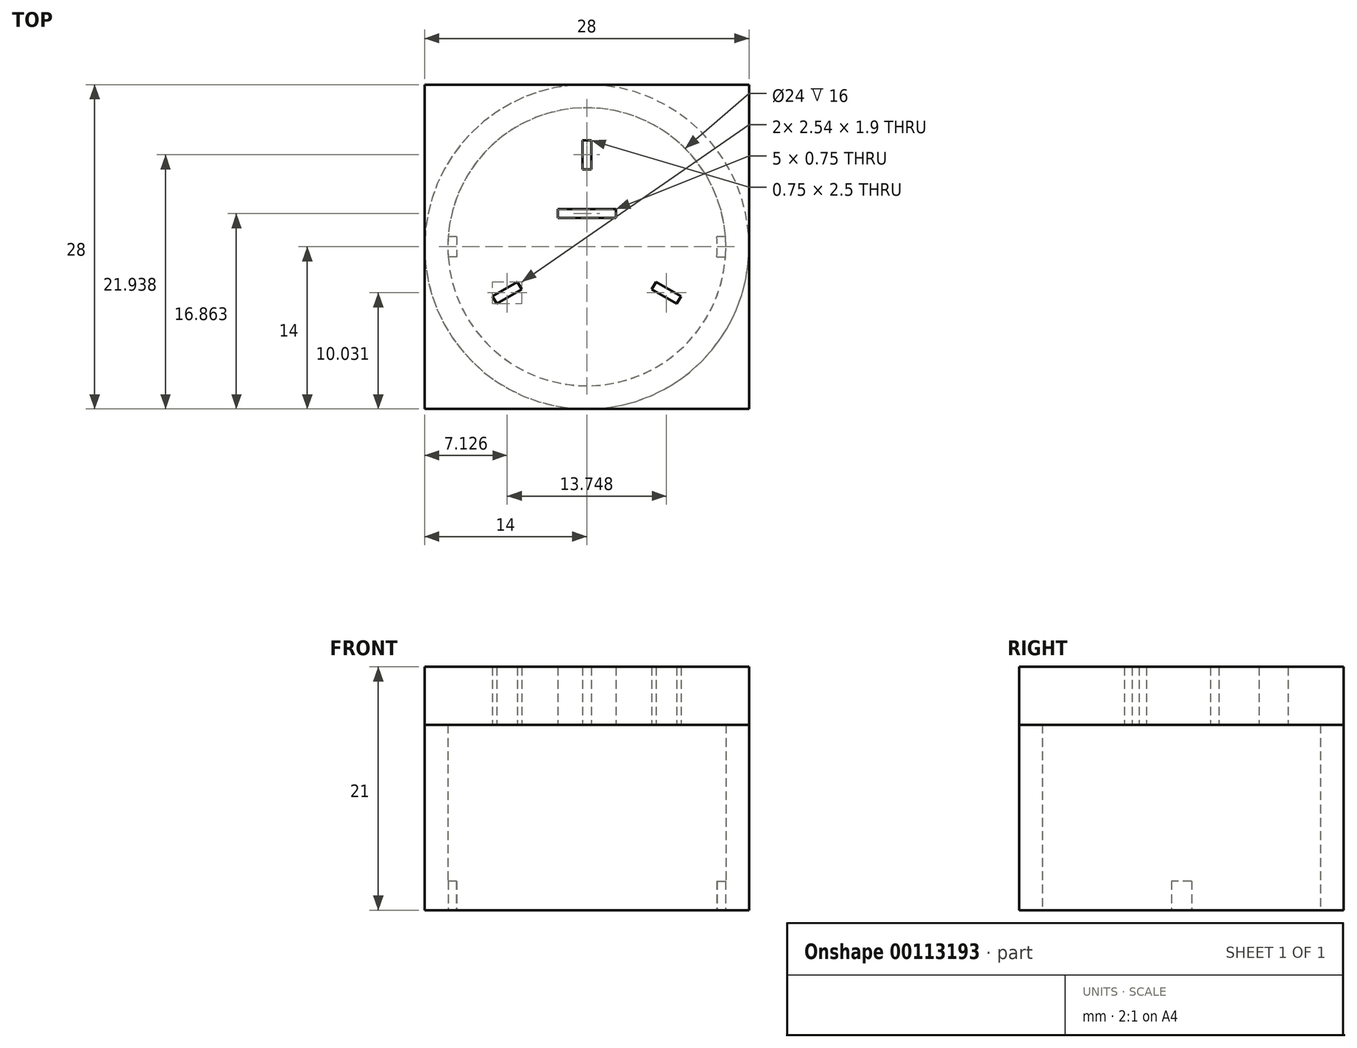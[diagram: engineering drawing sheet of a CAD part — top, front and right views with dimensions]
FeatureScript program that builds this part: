
annotation { "Feature Type Name" : "Feature", "Feature Type Description" : "" }
export const myFeature = defineFeature(function(context is Context, id is Id, definition is map)
    precondition{}
    {
        {
            var Q0;
            Q0=qCreatedBy(makeId("Top.planeOp"),FACE);
            var sketch = newSketch(context, id + "F0", { "sketchPlane" : qUnion([Q0])});
            skCircle(sketch, "E0", {"center": v(0, 0) * mm, "radius": 12 * mm});
            skCircle(sketch, "E1.0", {"center": v(0, 0) * mm, "radius": 14 * mm});
            skSolve(sketch);
        }
        {
            var Q0;
            Q0=makeQuery(id+"F0.imprint","IMPRINT",FACE,{"disambiguationData":[TD([[makeQuery(id+"F0.imprint","IMPRINT",EDGE,{"derivedFrom":sQuery(id+"F0.wireOp",EDGE,"E0")}),-1.0]])]});
            extrude(context, id + "F1", {"entities" : qUnion([Q0]), "depth" : 16 * mm});
        }
        {
            var Q0;
            Q0=qCreatedBy(makeId("Top.planeOp"),FACE);
            var sketch = newSketch(context, id + "F2", { "sketchPlane" : qUnion([Q0])});
            skLineSegment(sketch, "E2", {"start": v(12, 0) * mm, "end": v(-12, 0) * mm, "construction": true});
            skArc(sketch, "E3.0", {"start": v(-11.97, 0.87) * mm, "mid": v(-12, 0) * mm, "end": v(-11.97, -0.87) * mm});
            skLineSegment(sketch, "E4", {"start": v(11.97, 0.88) * mm, "end": v(11.22, 0.88) * mm});
            skLineSegment(sketch, "E5", {"start": v(11.22, -0.88) * mm, "end": v(11.97, -0.88) * mm});
            skArc(sketch, "E6", {"start": v(-11.22, 0.87) * mm, "mid": v(-11.25, 0) * mm, "end": v(-11.22, -0.87) * mm});
            skLineSegment(sketch, "E7", {"start": v(-11.22, 0.88) * mm, "end": v(-11.97, 0.88) * mm});
            skLineSegment(sketch, "E8", {"start": v(-11.22, -0.88) * mm, "end": v(-11.97, -0.88) * mm});
            skLineSegment(sketch, "E9", {"start": v(11.6, 0.87) * mm, "end": v(11.6, -0.88) * mm, "construction": true});
            skPoint(sketch, "E10", {"position": v(11.6, 0) * mm});
            skArc(sketch, "E11.trimOffspring", {"start": v(11.97, -0.87) * mm, "mid": v(12, 0) * mm, "end": v(11.97, 0.87) * mm});
            skArc(sketch, "E12.trimOffspring", {"start": v(11.22, -0.87) * mm, "mid": v(11.25, 0) * mm, "end": v(11.22, 0.88) * mm});
            skSolve(sketch);
        }
        {
            var Q0;
            Q0 = qSketchRegion(id + "F2", true);
            extrude(context, id + "F3", {"entities" : qUnion([Q0]), "operationType" : NewBodyOperationType.ADD, "depth" : 2.5 * mm});
        }
        {
            var Q0;
            Q0=makeQuery(id+"F1.opExtrude","CAP_FACE",FACE,{"disambiguationData":[OSD([sQuery(id+"F0.wireOp",EDGE,"E0"),sQuery(id+"F0.wireOp",EDGE,"E1.0")])],"isStart":false});
            var sketch = newSketch(context, id + "F4", { "sketchPlane" : qUnion([Q0])});
            skLineSegment(sketch, "E13.bottom", {"start": v(-14, -14) * mm, "end": v(14, -14) * mm});
            skLineSegment(sketch, "E13.top", {"start": v(-14, 14) * mm, "end": v(14, 14) * mm});
            skLineSegment(sketch, "E13.left", {"start": v(-14, -14) * mm, "end": v(-14, 14) * mm});
            skLineSegment(sketch, "E13.right", {"start": v(14, -14) * mm, "end": v(14, 14) * mm});
            skPoint(sketch, "E13.middle", {"position": v(0, 0) * mm});
            skSolve(sketch);
        }
        {
            var Q0;
            Q0 = qSketchRegion(id + "F4", true);
            extrude(context, id + "F5", {"entities" : qUnion([Q0]), "operationType" : NewBodyOperationType.ADD, "depth" : 5 * mm});
        }
        {
            var Q0;
            Q0=makeQuery(id+"F5.boolean.opBoolean","SPLIT",FACE,{"disambiguationData":[TD([makeQuery(id+"F1.opExtrude","SWEPT_FACE",FACE,{"disambiguationData":[OSD([sQuery(id+"F0.wireOp",EDGE,"E0")])]})])],"derivedFrom":makeQuery(id+"F5.opExtrude","CAP_FACE",FACE,{"disambiguationData":[OSD([sQuery(id+"F4.wireOp",EDGE,"E13.bottom"),sQuery(id+"F4.wireOp",EDGE,"E13.top"),sQuery(id+"F4.wireOp",EDGE,"E13.left"),sQuery(id+"F4.wireOp",EDGE,"E13.right")])],"isStart":true})});
            var sketch = newSketch(context, id + "F6", { "sketchPlane" : qUnion([Q0])});
            skLineSegment(sketch, "E14", {"start": v(0, 0) * mm, "end": v(0, -12) * mm, "construction": true});
            skCircle(sketch, "E15", {"center": v(0, 0) * mm, "radius": 4.92 * mm, "construction": true});
            skCircle(sketch, "E16", {"center": v(0, 0) * mm, "radius": 9.53 * mm, "construction": true});
            skCircle(sketch, "E17", {"center": v(0, 0) * mm, "radius": 6.35 * mm, "construction": true});
            skLineSegment(sketch, "E18.bottom", {"start": v(2.5, -2.49) * mm, "end": v(-2.5, -2.49) * mm});
            skLineSegment(sketch, "E18.top", {"start": v(2.5, -3.24) * mm, "end": v(-2.5, -3.24) * mm});
            skLineSegment(sketch, "E18.left", {"start": v(2.5, -2.49) * mm, "end": v(2.5, -3.24) * mm});
            skLineSegment(sketch, "E18.right", {"start": v(-2.5, -2.49) * mm, "end": v(-2.5, -3.24) * mm});
            skPoint(sketch, "E18.middle", {"position": v(0, -2.86) * mm});
            skLineSegment(sketch, "E19.bottom", {"start": v(0.38, -9.19) * mm, "end": v(-0.37, -9.19) * mm});
            skLineSegment(sketch, "E19.top", {"start": v(0.38, -6.69) * mm, "end": v(-0.37, -6.69) * mm});
            skLineSegment(sketch, "E19.left", {"start": v(0.37, -9.19) * mm, "end": v(0.37, -6.69) * mm});
            skLineSegment(sketch, "E19.right", {"start": v(-0.38, -9.19) * mm, "end": v(-0.38, -6.69) * mm});
            skPoint(sketch, "E19.middle", {"position": v(0, -7.94) * mm});
            skLineSegment(sketch, "E20", {"start": v(0, -6.35) * mm, "end": v(0, -9.53) * mm});
            skLineSegment(sketch, "E21.1.0", {"start": v(5.5, 3.17) * mm, "end": v(8.25, 4.76) * mm});
            skLineSegment(sketch, "E21.1.1", {"start": v(8.14, 4.27) * mm, "end": v(5.98, 3.02) * mm});
            skLineSegment(sketch, "E21.1.2", {"start": v(7.77, 4.92) * mm, "end": v(5.6, 3.67) * mm});
            skLineSegment(sketch, "E21.1.3", {"start": v(5.6, 3.67) * mm, "end": v(5.98, 3.02) * mm});
            skPoint(sketch, "E21.1.4", {"position": v(6.87, 3.97) * mm});
            skLineSegment(sketch, "E21.1.5", {"start": v(7.77, 4.92) * mm, "end": v(8.14, 4.27) * mm});
            skLineSegment(sketch, "E21.2.0", {"start": v(-5.5, 3.17) * mm, "end": v(-8.25, 4.76) * mm});
            skLineSegment(sketch, "E21.2.1", {"start": v(-7.77, 4.92) * mm, "end": v(-5.6, 3.67) * mm});
            skLineSegment(sketch, "E21.2.2", {"start": v(-8.14, 4.27) * mm, "end": v(-5.98, 3.02) * mm});
            skLineSegment(sketch, "E21.2.3", {"start": v(-5.98, 3.02) * mm, "end": v(-5.6, 3.67) * mm});
            skPoint(sketch, "E21.2.4", {"position": v(-6.87, 3.97) * mm});
            skLineSegment(sketch, "E21.2.5", {"start": v(-8.14, 4.27) * mm, "end": v(-7.77, 4.92) * mm});
            skSolve(sketch);
        }
        {
            var Q0;
            Q0 = qSketchRegion(id + "F6", true);
            extrude(context, id + "F7", {"entities" : qUnion([Q0]), "operationType" : NewBodyOperationType.REMOVE, "endBound" : BoundingType.THROUGH_ALL, "oppositeDirection" : true, "depth" : 25 * mm});
        }
    });
